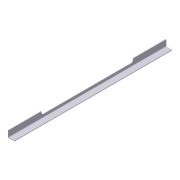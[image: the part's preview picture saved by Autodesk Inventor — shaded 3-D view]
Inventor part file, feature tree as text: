
AUTODESK INVENTOR PART (.ipt)
format: ipt  version: 2012 (Build 160160000, 160)  size: 89,600 bytes
history: native  units: in
note: dims shown in document units (in); Inventor stores cm internally (conversion verified against a paired STEP export)
features: extrude x2, sketch x2
ambient origin geometry x8: Origin, YZ Plane, XZ Plane, XY Plane, X Axis, Y Axis, Z Axis, Center Point
bodies: Solid1 (feature_tree)
feature tree (4):
  extrude  "Extrusion1"  Depth=3.0in
  extrude  "Extrusion2"  Depth=0.23in
  sketch  "Sketch1"  dims[d0=3.0in d1=3.0in]
  sketch  "Sketch2"  dims[d2=0.25in d3=0.23in d4=72.0in d5=0.0in d6=1.0in d7=1.5in d8=15.0in d9=15.0in d10=72.0in d11=0.0in]
